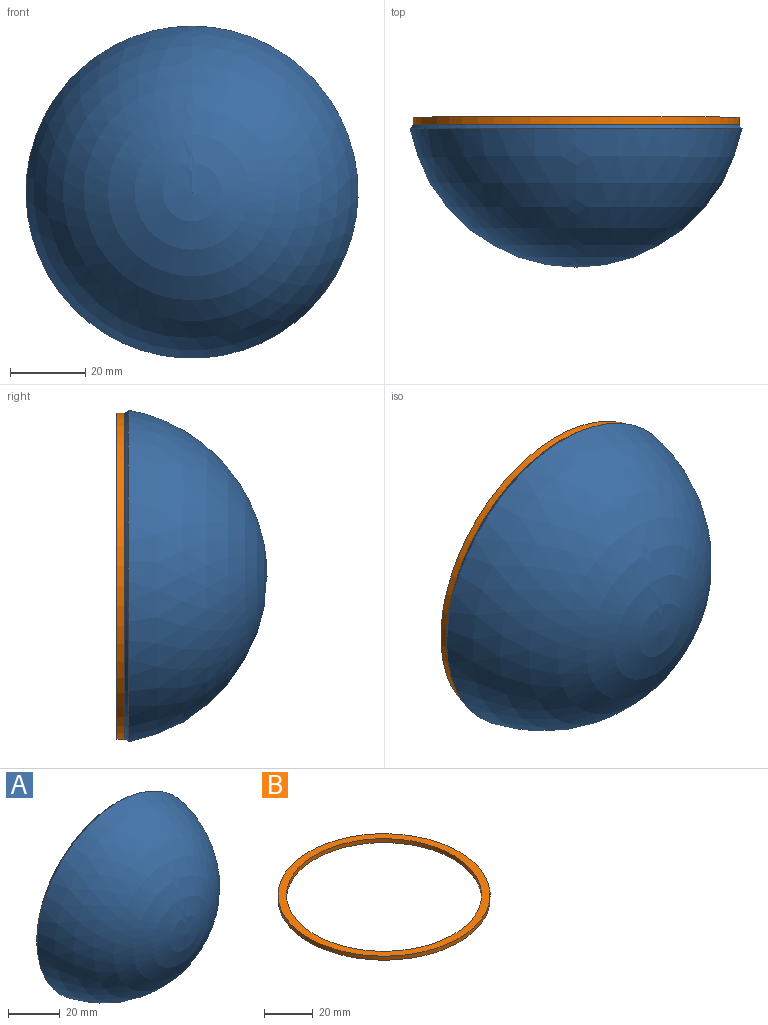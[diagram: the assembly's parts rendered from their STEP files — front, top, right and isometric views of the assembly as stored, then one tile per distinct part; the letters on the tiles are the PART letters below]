
ASSEMBLY  parts=2 mates=1
PART A: 3 faces, bbox 88.6x38x88.6 mm
  f0: plane 86.88x86.88mm, normal (0,1,0), area 5928.5mm2, adj f2
  f1: sphere r=45mm, area 10459.5mm2, adj f2
  f2: cone r=44.28mm half-angle=39.9deg, axis (0,-1,0), area 361.6mm2, adj f0,f1
PART B: 4 faces, bbox 87x87x2 mm
  f0: cylinder r=43.5mm len=87mm, axis (0,0,-1), area 546.6mm2, adj f2,f3
  f1: cylinder r=40mm len=80mm, axis (0,0,-1), area 502.7mm2, adj f2,f3
  f2: plane 87x87mm, normal (0,0,1), area 918.1mm2, adj f0,f1
  f3: plane 87x87mm, normal (0,0,-1), area 918.1mm2, adj f0,f1
PLACE A t=(0.03,25.77,-0.54)mm
PLACE B rot(axis=(-1,0,0),90deg) t=(0.03,18.77,-0.54)mm
MATE planar B.f0 <-> A.f2  axis (0,-1,0) through (0.03,18.77,-0.54)mm
